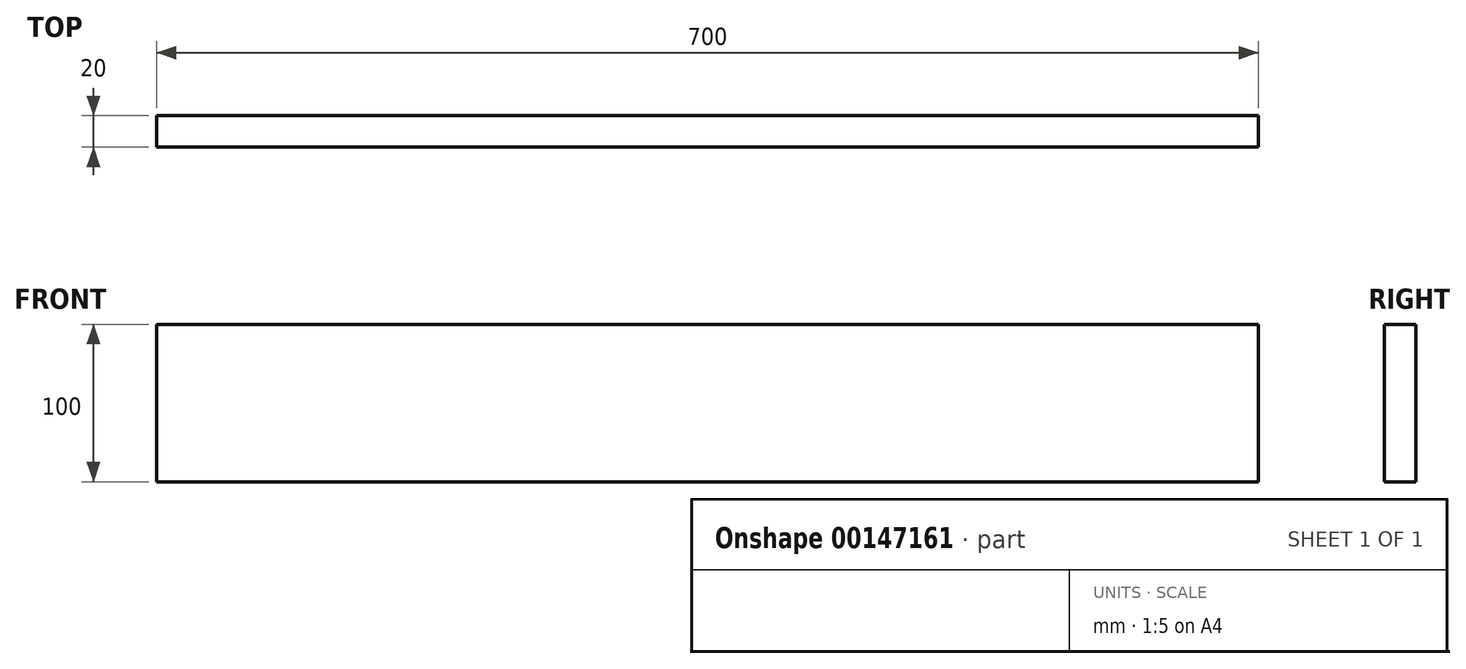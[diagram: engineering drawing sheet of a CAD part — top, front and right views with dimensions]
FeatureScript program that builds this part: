
annotation { "Feature Type Name" : "Feature", "Feature Type Description" : "" }
export const myFeature = defineFeature(function(context is Context, id is Id, definition is map)
    precondition{}
    {
        {
            var Q0;
            Q0=qCreatedBy(makeId("Right.planeOp"),FACE);
            var sketch = newSketch(context, id + "F0", { "sketchPlane" : qUnion([Q0])});
            skLineSegment(sketch, "E0.bottom", {"start": v(10, -50) * mm, "end": v(-10, -50) * mm});
            skLineSegment(sketch, "E0.top", {"start": v(10, 50) * mm, "end": v(-10, 50) * mm});
            skLineSegment(sketch, "E0.left", {"start": v(10, -50) * mm, "end": v(10, 50) * mm});
            skLineSegment(sketch, "E0.right", {"start": v(-10, -50) * mm, "end": v(-10, 50) * mm});
            skPoint(sketch, "E0.middle", {"position": v(0, 0) * mm});
            skSolve(sketch);
        }
        {
            var Q0;
            Q0=makeQuery(id+"F0.imprint","IMPRINT",FACE,{"disambiguationData":[TD([[makeQuery(id+"F0.imprint","IMPRINT",EDGE,{"derivedFrom":sQuery(id+"F0.wireOp",EDGE,"E0.bottom")}),-1.0]])]});
            extrude(context, id + "F1", {"entities" : qUnion([Q0]), "depth" : 700 * mm});
        }
    });
